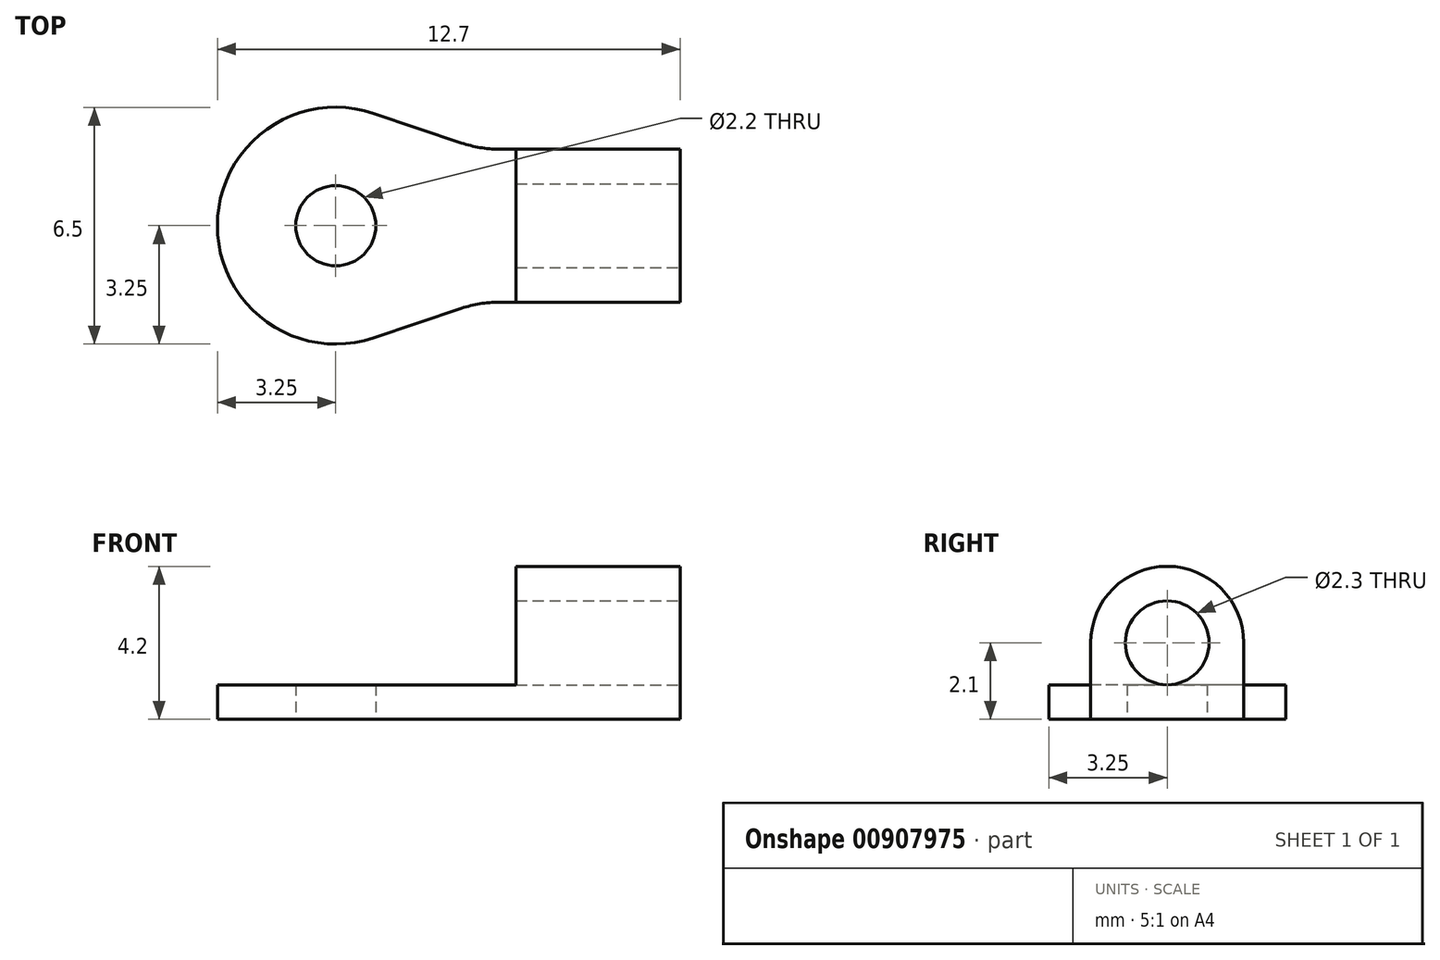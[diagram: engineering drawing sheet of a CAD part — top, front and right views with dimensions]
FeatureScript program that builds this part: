
annotation { "Feature Type Name" : "Feature", "Feature Type Description" : "" }
export const myFeature = defineFeature(function(context is Context, id is Id, definition is map)
    precondition{}
    {
        {
            var Q0;
            Q0=qCreatedBy(makeId("Top.planeOp"),FACE);
            var sketch = newSketch(context, id + "F0", { "sketchPlane" : qUnion([Q0])});
            skLineSegment(sketch, "E0.left", {"start": v(0, 3.25) * mm, "end": v(0, 3.25) * mm});
            skLineSegment(sketch, "E0.right", {"start": v(12.7, 1.15) * mm, "end": v(12.7, 5.35) * mm});
            skPoint(sketch, "E1.visualSharp", {"position": v(0, 6.5) * mm});
            skArc(sketch, "E1.filletArc", {"start": v(3.25, 6.5) * mm, "mid": v(0.95, 5.55) * mm, "end": v(0, 3.25) * mm});
            skPoint(sketch, "E2.visualSharp", {"position": v(0, 0) * mm});
            skArc(sketch, "E2.filletArc", {"start": v(0, 3.25) * mm, "mid": v(0.95, 0.95) * mm, "end": v(3.25, 0) * mm});
            skArc(sketch, "E3", {"start": v(4.29, 6.33) * mm, "mid": v(0, 3.25) * mm, "end": v(4.29, 0.17) * mm});
            skCircle(sketch, "E4", {"center": v(3.25, 3.25) * mm, "radius": 1.1 * mm});
            skLineSegment(sketch, "E5.bottom", {"start": v(7.73, 1.15) * mm, "end": v(12.7, 1.15) * mm});
            skLineSegment(sketch, "E5.top", {"start": v(7.73, 5.35) * mm, "end": v(12.7, 5.35) * mm});
            skPoint(sketch, "E5.middle", {"position": v(12.7, 3.25) * mm});
            skLineSegment(sketch, "E6", {"start": v(6.7, 5.52) * mm, "end": v(4.29, 6.33) * mm});
            skLineSegment(sketch, "E7", {"start": v(6.7, 0.98) * mm, "end": v(4.29, 0.17) * mm});
            skPoint(sketch, "E8.visualSharp", {"position": v(7.2, 5.35) * mm});
            skArc(sketch, "E8.filletArc", {"start": v(6.7, 5.52) * mm, "mid": v(7.2, 5.4) * mm, "end": v(7.73, 5.35) * mm});
            skPoint(sketch, "E9.visualSharp", {"position": v(7.2, 1.15) * mm});
            skArc(sketch, "E9.filletArc", {"start": v(7.73, 1.15) * mm, "mid": v(7.2, 1.1) * mm, "end": v(6.7, 0.98) * mm});
            skPoint(sketch, "E10.orphan", {"position": v(17.2, 5.35) * mm});
            skPoint(sketch, "E11.orphan", {"position": v(17.2, 1.15) * mm});
            skPoint(sketch, "E12.orphan", {"position": v(12.7, 6.5) * mm});
            skPoint(sketch, "E0.bottom.end.orphan", {"position": v(12.7, 0) * mm});
            skPoint(sketch, "E5.left.end.orphan", {"position": v(8.2, 5.35) * mm});
            skPoint(sketch, "E5.left.start.orphan", {"position": v(8.2, 1.15) * mm});
            skSolve(sketch);
        }
        {
            var Q0;
            Q0=makeQuery(id+"F0.imprint","IMPRINT",FACE,{"disambiguationData":[TD([[makeQuery(id+"F0.imprint","IMPRINT",EDGE,{"derivedFrom":sQuery(id+"F0.wireOp",EDGE,"E0.right")}),1.0]])]});
            extrude(context, id + "F1", {"entities" : qUnion([Q0]), "depth" : 0.95 * mm, "offsetDistance" : 25 * mm});
        }
        {
            var Q0;
            Q0=makeQuery(id+"F1.opExtrude","CAP_FACE",FACE,{"disambiguationData":[OSD([sQuery(id+"F0.wireOp",EDGE,"E0.right"),sQuery(id+"F0.wireOp",EDGE,"E3"),sQuery(id+"F0.wireOp",EDGE,"E4"),sQuery(id+"F0.wireOp",EDGE,"E5.bottom"),sQuery(id+"F0.wireOp",EDGE,"E5.top"),sQuery(id+"F0.wireOp",EDGE,"E6"),sQuery(id+"F0.wireOp",EDGE,"E7"),sQuery(id+"F0.wireOp",EDGE,"E8.filletArc"),sQuery(id+"F0.wireOp",EDGE,"E9.filletArc")])],"isStart":false});
            var sketch = newSketch(context, id + "F2", { "sketchPlane" : qUnion([Q0])});
            skPoint(sketch, "E13.middle", {"position": v(12.7, 3.25) * mm});
            skLineSegment(sketch, "E14.bottom", {"start": v(12.7, 5.35) * mm, "end": v(8.2, 5.35) * mm});
            skLineSegment(sketch, "E14.top", {"start": v(12.7, 1.15) * mm, "end": v(8.2, 1.15) * mm});
            skLineSegment(sketch, "E14.left", {"start": v(12.7, 5.35) * mm, "end": v(12.7, 1.15) * mm});
            skLineSegment(sketch, "E14.right", {"start": v(8.2, 5.35) * mm, "end": v(8.2, 1.15) * mm});
            skSolve(sketch);
        }
        {
            var Q0;
            Q0=makeQuery(id+"F2.imprint","IMPRINT",FACE,{"disambiguationData":[TD([[makeQuery(id+"F2.imprint","IMPRINT",EDGE,{"derivedFrom":sQuery(id+"F2.wireOp",EDGE,"E14.bottom")}),-1.0]])]});
            extrude(context, id + "F3", {"entities" : qUnion([Q0]), "operationType" : NewBodyOperationType.ADD, "depth" : 3.25 * mm, "offsetDistance" : 25 * mm});
        }
        {
            var Q0;
            Q0=makeQuery(id+"F3.opExtrude","CAP_EDGE",EDGE,{"disambiguationData":[OSD([sQuery(id+"F2.wireOp",EDGE,"E14.bottom")])],"isStart":false});
            var Q1;
            Q1=makeQuery(id+"F3.opExtrude","CAP_EDGE",EDGE,{"disambiguationData":[OSD([sQuery(id+"F2.wireOp",EDGE,"E14.top")])],"isStart":false});
            fillet(context, id + "F4", {"entities" : qUnion([Q0, Q1]), "radius" : 2.1 * mm, "tangentPropagation" : true, "allowEdgeOverflow" : false});
        }
        {
            var Q0;
            Q0=makeQuery(id+"F3.boolean.opBoolean","MERGE",FACE,{"derivedFrom":[makeQuery(id+"F1.opExtrude","SWEPT_FACE",FACE,{"disambiguationData":[OSD([sQuery(id+"F0.wireOp",EDGE,"E0.right")])]}),makeQuery(id+"F3.opExtrude","SWEPT_FACE",FACE,{"disambiguationData":[OSD([sQuery(id+"F2.wireOp",EDGE,"E14.left")])]})]});
            var sketch = newSketch(context, id + "F5", { "sketchPlane" : qUnion([Q0])});
            skCircle(sketch, "E15", {"center": v(3.25, 2.1) * mm, "radius": 1.15 * mm});
            skSolve(sketch);
        }
        {
            var Q0;
            Q0=makeQuery(id+"F5.imprint","IMPRINT",FACE,{"disambiguationData":[TD([[makeQuery(id+"F5.imprint","IMPRINT",EDGE,{"derivedFrom":sQuery(id+"F5.wireOp",EDGE,"E15")}),1.0]])]});
            extrude(context, id + "F6", {"entities" : qUnion([Q0]), "operationType" : NewBodyOperationType.REMOVE, "oppositeDirection" : true, "depth" : 25 * mm, "offsetDistance" : 25 * mm});
        }
    });
